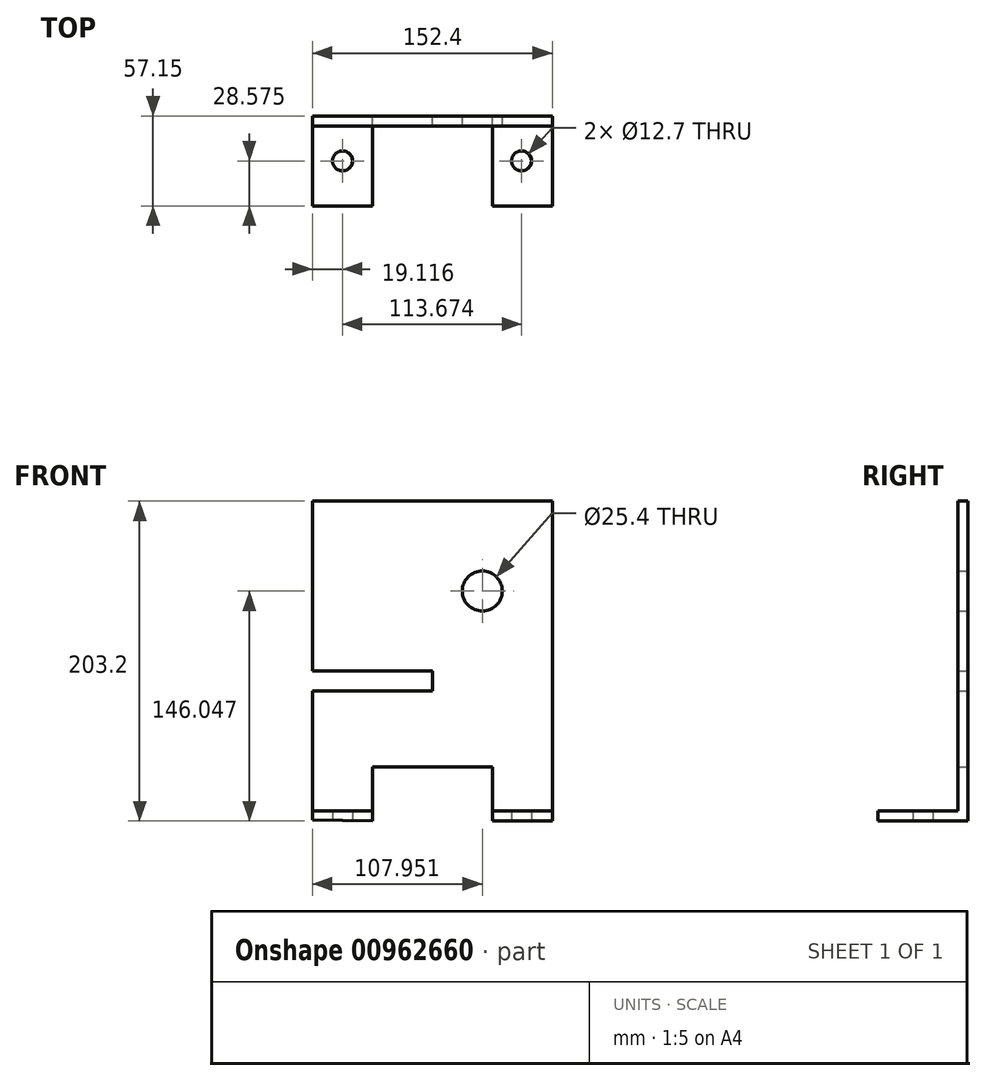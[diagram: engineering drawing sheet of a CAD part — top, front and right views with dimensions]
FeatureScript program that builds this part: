
annotation { "Feature Type Name" : "Feature", "Feature Type Description" : "" }
export const myFeature = defineFeature(function(context is Context, id is Id, definition is map)
    precondition{}
    {
        {
            var Q0;
            Q0=qCreatedBy(makeId("Front.planeOp"),FACE);
            var sketch = newSketch(context, id + "F0", { "sketchPlane" : qUnion([Q0])});
            skCircle(sketch, "E0", {"center": v(41.03, 70.84) * mm, "radius": 12.7 * mm});
            skLineSegment(sketch, "E1", {"start": v(-66.92, 127.99) * mm, "end": v(85.48, 127.99) * mm});
            skLineSegment(sketch, "E2", {"start": v(85.48, 127.99) * mm, "end": v(85.48, -75.21) * mm});
            skLineSegment(sketch, "E3", {"start": v(85.48, -75.21) * mm, "end": v(47.38, -75.21) * mm});
            skLineSegment(sketch, "E4", {"start": v(47.38, -75.21) * mm, "end": v(47.38, -40.76) * mm});
            skLineSegment(sketch, "E5", {"start": v(47.38, -40.76) * mm, "end": v(-28.82, -40.76) * mm});
            skLineSegment(sketch, "E6", {"start": v(-28.82, -40.76) * mm, "end": v(-28.82, -75.21) * mm});
            skLineSegment(sketch, "E7", {"start": v(-66.92, 127.99) * mm, "end": v(-66.92, 20.04) * mm});
            skLineSegment(sketch, "E8", {"start": v(-66.92, 20.04) * mm, "end": v(9.28, 20.04) * mm});
            skLineSegment(sketch, "E9", {"start": v(9.28, 20.04) * mm, "end": v(9.28, 7.34) * mm});
            skLineSegment(sketch, "E10", {"start": v(9.28, 7.34) * mm, "end": v(-66.92, 7.34) * mm});
            skLineSegment(sketch, "E11", {"start": v(-66.92, 7.34) * mm, "end": v(-66.92, -74.4) * mm});
            skLineSegment(sketch, "E12", {"start": v(-66.92, -74.4) * mm, "end": v(-28.82, -75.21) * mm});
            skSolve(sketch);
        }
        {
            var Q0;
            Q0=qSketchRegion(id+"F0",true);
            extrude(context, id + "F1", {"entities" : qUnion([Q0]), "depth" : 6.35 * mm, "offsetDistance" : 25.4 * mm});
        }
        {
            var Q0;
            Q0=makeQuery(id+"F1.opExtrude","CAP_FACE",FACE,{"disambiguationData":[OSD([sQuery(id+"F0.wireOp",EDGE,"E0"),sQuery(id+"F0.wireOp",EDGE,"E1"),sQuery(id+"F0.wireOp",EDGE,"E2"),sQuery(id+"F0.wireOp",EDGE,"E3"),sQuery(id+"F0.wireOp",EDGE,"E4"),sQuery(id+"F0.wireOp",EDGE,"E5"),sQuery(id+"F0.wireOp",EDGE,"E6"),sQuery(id+"F0.wireOp",EDGE,"E7"),sQuery(id+"F0.wireOp",EDGE,"E8"),sQuery(id+"F0.wireOp",EDGE,"E9"),sQuery(id+"F0.wireOp",EDGE,"E10"),sQuery(id+"F0.wireOp",EDGE,"E11"),sQuery(id+"F0.wireOp",EDGE,"E12")])],"isStart":false});
            var sketch = newSketch(context, id + "F2", { "sketchPlane" : qUnion([Q0])});
            skLineSegment(sketch, "E13", {"start": v(-66.92, -68.86) * mm, "end": v(-28.82, -68.86) * mm});
            skLineSegment(sketch, "E14", {"start": v(47.38, -68.86) * mm, "end": v(85.48, -68.86) * mm});
            skSolve(sketch);
        }
        {
            var Q0;
            Q0=qSketchRegion(id+"F2",true);
            var Q1;
            {var subQ0=sQuery(id+"F2.wireOp",EDGE,"E13");Q1=makeQuery(id+"F2.imprint","IMPRINT",FACE,{"disambiguationData":[TD([[makeQuery(id+"F2.imprint","IMPRINT",EDGE,{"derivedFrom":subQ0}),-1.0]])]});}
            var Q2;
            {var subQ0=sQuery(id+"F2.wireOp",EDGE,"E14");Q2=makeQuery(id+"F2.imprint","IMPRINT",FACE,{"disambiguationData":[TD([[makeQuery(id+"F2.imprint","IMPRINT",EDGE,{"derivedFrom":subQ0}),-1.0]])]});}
            extrude(context, id + "F3", {"entities" : qUnion([Q0, Q1, Q2]), "operationType" : NewBodyOperationType.ADD, "depth" : 50.8 * mm, "offsetDistance" : 25.4 * mm});
        }
        {
            var Q0;
            {var subQ0=sQuery(id+"F0.wireOp",EDGE,"E12");Q0=makeQuery(id+"F3.boolean.opBoolean","MERGE",FACE,{"derivedFrom":[makeQuery(id+"F1.opExtrude","SWEPT_FACE",FACE,{"disambiguationData":[OSD([subQ0])]}),makeQuery(id+"F3.opExtrude","SWEPT_FACE",FACE,{"disambiguationData":[OSD([subQ0])]})]});}
            var sketch = newSketch(context, id + "F4", { "sketchPlane" : qUnion([Q0])});
            skCircle(sketch, "E15", {"center": v(-46.26, 28.57) * mm, "radius": 6.35 * mm});
            skPoint(sketch, "E15.centerSnap0", {"position": v(-46.26, 57.15) * mm});
            skPoint(sketch, "E15.centerSnap1", {"position": v(-65.32, 28.57) * mm});
            skCircle(sketch, "E16", {"center": v(67.39, 28.57) * mm, "radius": 6.35 * mm});
            skPoint(sketch, "E16.centerSnap0", {"position": v(-27.2, 28.57) * mm});
            skSolve(sketch);
        }
        {
            var Q0;
            Q0=makeQuery(id+"F4.imprint","IMPRINT",FACE,{"disambiguationData":[TD([[makeQuery(id+"F4.imprint","IMPRINT",EDGE,{"derivedFrom":sQuery(id+"F4.wireOp",EDGE,"E15")}),1.0]])]});
            var Q1;
            Q1=makeQuery(id+"F4.imprint","IMPRINT",FACE,{"disambiguationData":[TD([[makeQuery(id+"F4.imprint","IMPRINT",EDGE,{"derivedFrom":sQuery(id+"F4.wireOp",EDGE,"E16")}),1.0]])]});
            extrude(context, id + "F5", {"entities" : qUnion([Q0, Q1]), "operationType" : NewBodyOperationType.REMOVE, "oppositeDirection" : true, "depth" : 25.4 * mm, "offsetDistance" : 25.4 * mm});
        }
    });
